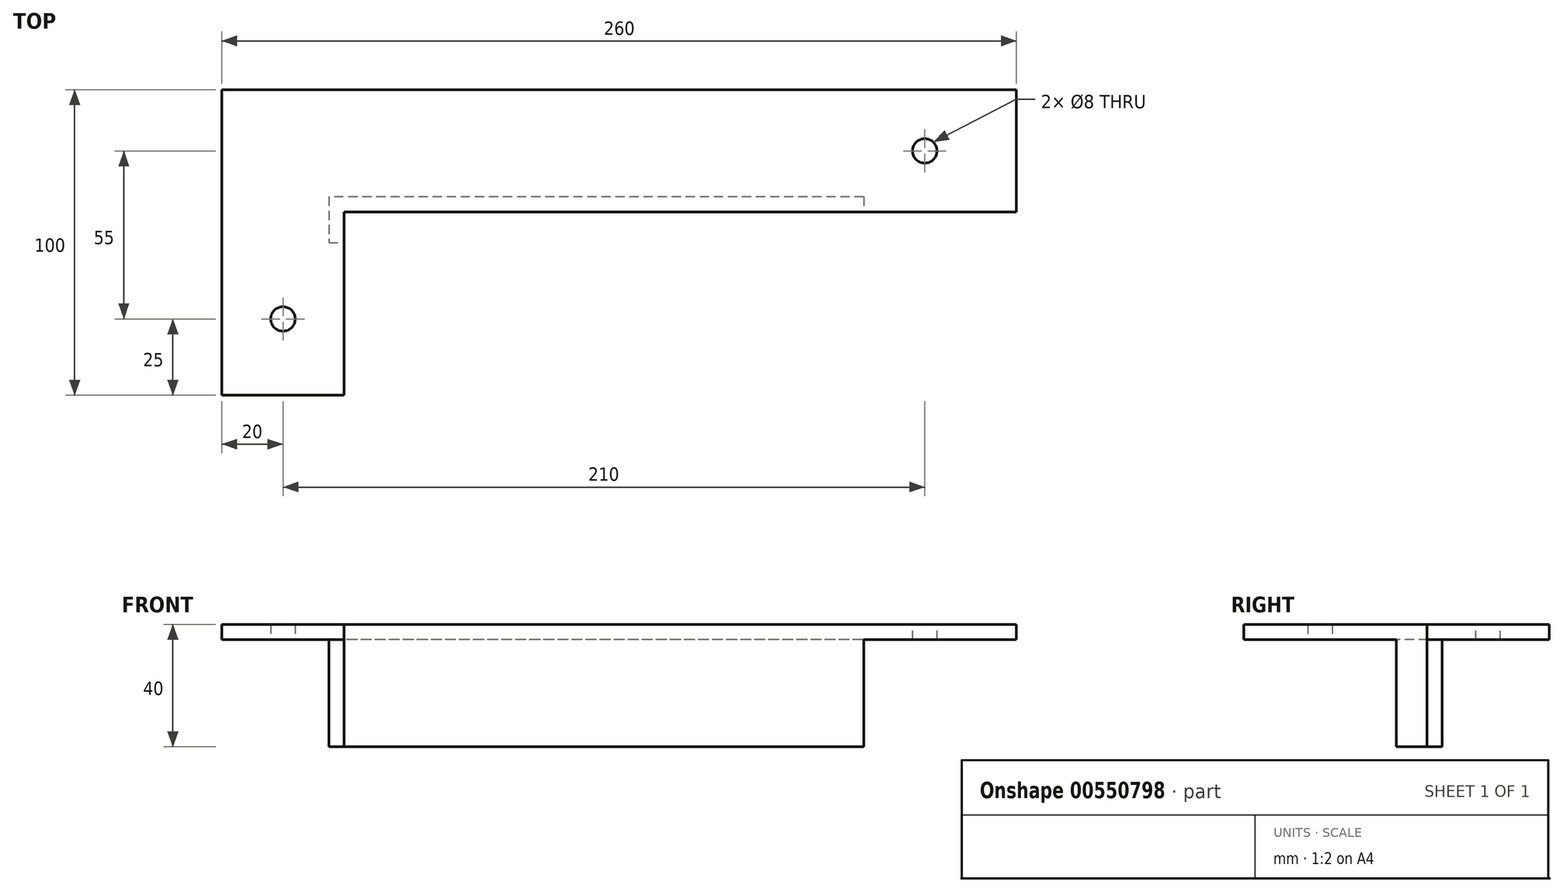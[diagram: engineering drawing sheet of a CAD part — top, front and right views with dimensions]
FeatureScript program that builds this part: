
annotation { "Feature Type Name" : "Feature", "Feature Type Description" : "" }
export const myFeature = defineFeature(function(context is Context, id is Id, definition is map)
    precondition{}
    {
        {
            var Q0;
            Q0=qCreatedBy(makeId("Top.planeOp"),FACE);
            var sketch = newSketch(context, id + "F0", { "sketchPlane" : qUnion([Q0])});
            skLineSegment(sketch, "E0.bottom", {"start": v(130, -20) * mm, "end": v(-130, -20) * mm});
            skLineSegment(sketch, "E0.top", {"start": v(130, 20) * mm, "end": v(-130, 20) * mm});
            skLineSegment(sketch, "E0.left", {"start": v(130, -20) * mm, "end": v(130, 20) * mm});
            skLineSegment(sketch, "E0.right", {"start": v(-130, -20) * mm, "end": v(-130, 20) * mm});
            skPoint(sketch, "E0.middle", {"position": v(0, 0) * mm});
            skSolve(sketch);
        }
        {
            var Q0;
            Q0=makeQuery(id+"F0.imprint","IMPRINT",FACE,{"disambiguationData":[TD([[makeQuery(id+"F0.imprint","IMPRINT",EDGE,{"derivedFrom":sQuery(id+"F0.wireOp",EDGE,"E0.bottom")}),-1.0]])]});
            extrude(context, id + "F1", {"entities" : qUnion([Q0]), "depth" : 5 * mm, "offsetDistance" : 25 * mm});
        }
        {
            var Q0;
            Q0=makeQuery(id+"F1.opExtrude","CAP_FACE",FACE,{"disambiguationData":[OSD([sQuery(id+"F0.wireOp",EDGE,"E0.bottom"),sQuery(id+"F0.wireOp",EDGE,"E0.top"),sQuery(id+"F0.wireOp",EDGE,"E0.left"),sQuery(id+"F0.wireOp",EDGE,"E0.right")])],"isStart":true});
            var sketch = newSketch(context, id + "F2", { "sketchPlane" : qUnion([Q0])});
            skLineSegment(sketch, "E1", {"start": v(130, 20) * mm, "end": v(80, 20) * mm});
            skLineSegment(sketch, "E2", {"start": v(80, 15) * mm, "end": v(80, 20) * mm});
            skLineSegment(sketch, "E3", {"start": v(80, 15) * mm, "end": v(-90, 15) * mm});
            skLineSegment(sketch, "E4", {"start": v(-90, 15) * mm, "end": v(-90, 20) * mm});
            skSolve(sketch);
        }
        {
            var Q0;
            Q0=qSketchRegion(id+"F2",true);
            var Q1;
            {var subQ0=sQuery(id+"F2.wireOp",EDGE,"E2");Q1=makeQuery(id+"F2.imprint","IMPRINT",FACE,{"disambiguationData":[TD([[makeQuery(id+"F2.imprint","IMPRINT",EDGE,{"derivedFrom":subQ0}),1.0]])]});}
            extrude(context, id + "F3", {"entities" : qUnion([Q0, Q1]), "operationType" : NewBodyOperationType.ADD, "depth" : 35 * mm, "offsetDistance" : 25 * mm});
        }
        {
            var Q0;
            Q0=makeQuery(id+"F1.opExtrude","CAP_FACE",FACE,{"disambiguationData":[OSD([sQuery(id+"F0.wireOp",EDGE,"E0.bottom"),sQuery(id+"F0.wireOp",EDGE,"E0.top"),sQuery(id+"F0.wireOp",EDGE,"E0.left"),sQuery(id+"F0.wireOp",EDGE,"E0.right")])],"isStart":true});
            var sketch = newSketch(context, id + "F4", { "sketchPlane" : qUnion([Q0])});
            skLineSegment(sketch, "E5", {"start": v(-130, 20) * mm, "end": v(-130, 80) * mm});
            skLineSegment(sketch, "E6", {"start": v(-130, 80) * mm, "end": v(-90, 80) * mm});
            skLineSegment(sketch, "E7", {"start": v(-90, 80) * mm, "end": v(-90, 20) * mm});
            skCircle(sketch, "E8", {"center": v(-110, 55) * mm, "radius": 4 * mm});
            skLineSegment(sketch, "E9", {"start": v(-110, 80) * mm, "end": v(-110, 55) * mm});
            skSolve(sketch);
        }
        {
            var Q0;
            Q0=qSketchRegion(id+"F4",true);
            var Q1;
            Q1=makeQuery(id+"F4.imprint","IMPRINT",FACE,{"disambiguationData":[TD([[makeQuery(id+"F4.imprint","IMPRINT",EDGE,{"derivedFrom":sQuery(id+"F4.wireOp",EDGE,"E5")}),-1.0]])]});
            extrude(context, id + "F5", {"entities" : qUnion([Q0, Q1]), "operationType" : NewBodyOperationType.ADD, "oppositeDirection" : true, "depth" : 5 * mm, "offsetDistance" : 25 * mm});
        }
        {
            var Q0;
            {var subQ0=sQuery(id+"F0.wireOp",EDGE,"E0.bottom");Q0=makeQuery(id+"F5.boolean.opBoolean","MERGE",FACE,{"derivedFrom":[makeQuery(id+"F1.opExtrude","CAP_FACE",FACE,{"disambiguationData":[OSD([subQ0,sQuery(id+"F0.wireOp",EDGE,"E0.top"),sQuery(id+"F0.wireOp",EDGE,"E0.left"),sQuery(id+"F0.wireOp",EDGE,"E0.right")])],"isStart":true}),makeQuery(id+"F5.opExtrude","CAP_FACE",FACE,{"disambiguationData":[OSD([subQ0,sQuery(id+"F4.wireOp",EDGE,"E5"),sQuery(id+"F4.wireOp",EDGE,"E6"),sQuery(id+"F4.wireOp",EDGE,"E7")])],"isStart":true})]});}
            var sketch = newSketch(context, id + "F6", { "sketchPlane" : qUnion([Q0])});
            skLineSegment(sketch, "E10", {"start": v(-90, 15) * mm, "end": v(-95, 15) * mm});
            skLineSegment(sketch, "E11", {"start": v(-95, 15) * mm, "end": v(-95, 30) * mm});
            skLineSegment(sketch, "E12", {"start": v(-95, 30) * mm, "end": v(-90, 30) * mm});
            skSolve(sketch);
        }
        {
            var Q0;
            Q0=qSketchRegion(id+"F6",true);
            var Q1;
            Q1=makeQuery(id+"F6.imprint","IMPRINT",FACE,{"disambiguationData":[TD([[makeQuery(id+"F6.imprint","IMPRINT",EDGE,{"derivedFrom":sQuery(id+"F6.wireOp",EDGE,"E10")}),-1.0]])]});
            extrude(context, id + "F7", {"entities" : qUnion([Q0, Q1]), "operationType" : NewBodyOperationType.ADD, "depth" : 35 * mm, "offsetDistance" : 25 * mm});
        }
        {
            var Q0;
            {var subQ0=sQuery(id+"F0.wireOp",EDGE,"E0.bottom");Q0=makeQuery(id+"F5.boolean.opBoolean","MERGE",FACE,{"derivedFrom":[makeQuery(id+"F1.opExtrude","CAP_FACE",FACE,{"disambiguationData":[OSD([subQ0,sQuery(id+"F0.wireOp",EDGE,"E0.top"),sQuery(id+"F0.wireOp",EDGE,"E0.left"),sQuery(id+"F0.wireOp",EDGE,"E0.right")])],"isStart":false}),makeQuery(id+"F5.opExtrude","CAP_FACE",FACE,{"disambiguationData":[OSD([subQ0,sQuery(id+"F4.wireOp",EDGE,"E5"),sQuery(id+"F4.wireOp",EDGE,"E6"),sQuery(id+"F4.wireOp",EDGE,"E7")])],"isStart":false})]});}
            var sketch = newSketch(context, id + "F8", { "sketchPlane" : qUnion([Q0])});
            skCircle(sketch, "E13", {"center": v(-110, -150) * mm, "radius": 4 * mm});
            skCircle(sketch, "E14", {"center": v(100, 0) * mm, "radius": 4 * mm});
            skSolve(sketch);
        }
        {
            var Q0;
            Q0=makeQuery(id+"F8.imprint","IMPRINT",FACE,{"disambiguationData":[TD([[makeQuery(id+"F8.imprint","IMPRINT",EDGE,{"derivedFrom":sQuery(id+"F8.wireOp",EDGE,"E13")}),1.0]])]});
            var Q1;
            Q1=makeQuery(id+"F8.imprint","IMPRINT",FACE,{"disambiguationData":[TD([[makeQuery(id+"F8.imprint","IMPRINT",EDGE,{"derivedFrom":sQuery(id+"F8.wireOp",EDGE,"E14")}),1.0]])]});
            var Q2;
            Q2=sQuery(id+"F8.wireOp",EDGE,"E13");
            var Q3;
            Q3=sQuery(id+"F8.wireOp",EDGE,"E14");
            extrude(context, id + "F9", {"entities" : qUnion([Q0, Q1]), "operationType" : NewBodyOperationType.REMOVE, "surfaceEntities" : qUnion([Q2, Q3]), "oppositeDirection" : true, "depth" : 25 * mm, "offsetDistance" : 25 * mm});
        }
        {
            var Q0;
            Q0 = qSketchRegion(id + "F4", true);
            extrude(context, id + "F10", {"entities" : qUnion([Q0]), "operationType" : NewBodyOperationType.REMOVE, "oppositeDirection" : true, "depth" : 25 * mm, "offsetDistance" : 25 * mm});
        }
    });
